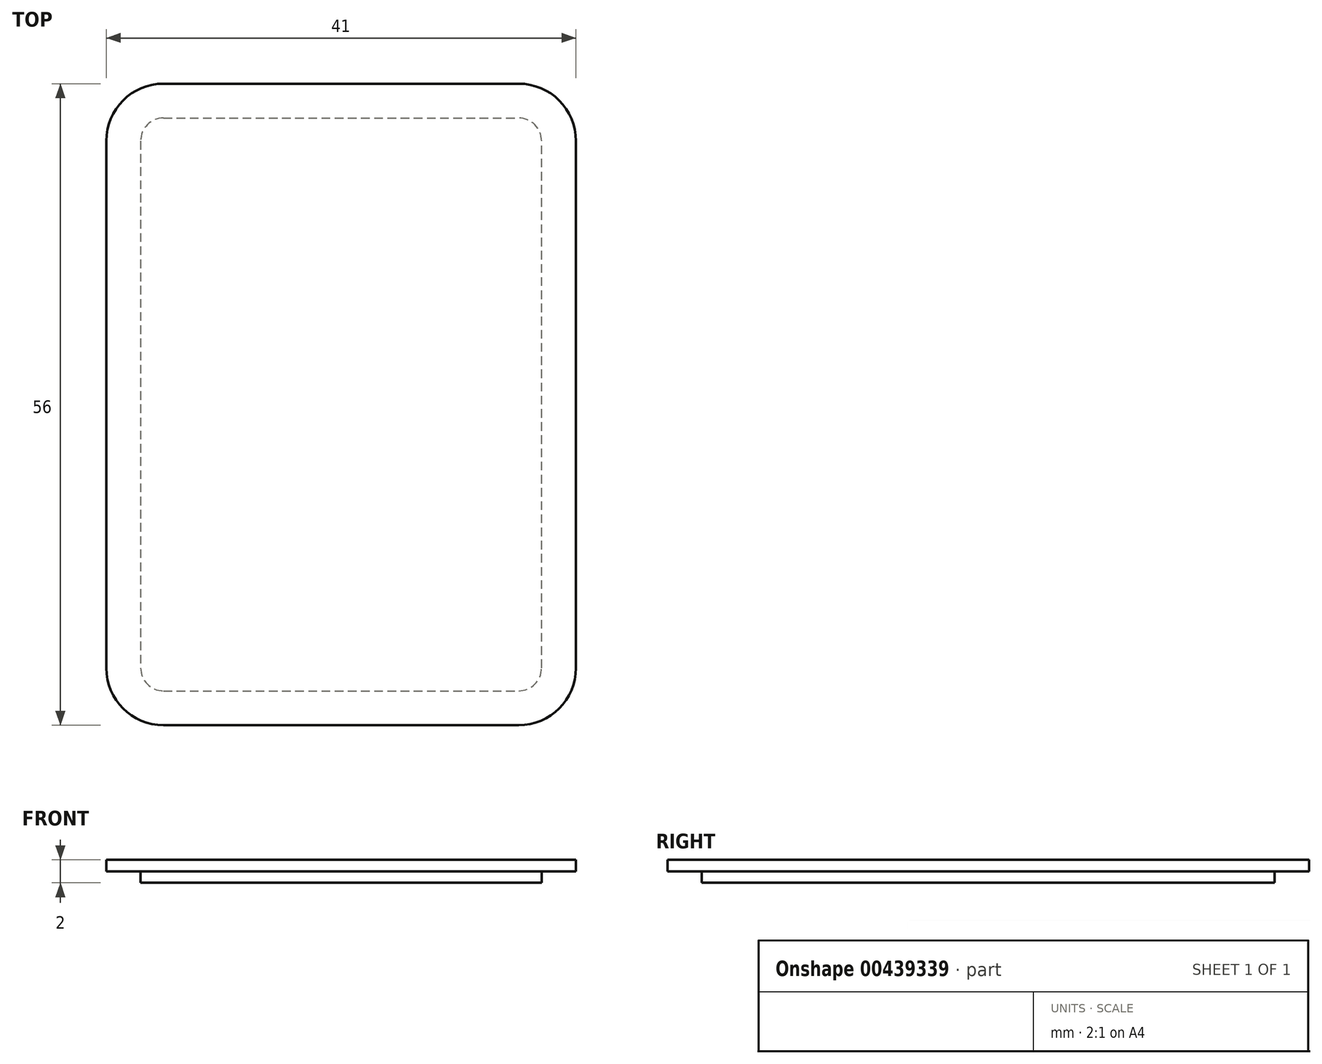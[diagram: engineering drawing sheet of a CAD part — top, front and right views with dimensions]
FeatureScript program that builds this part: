
annotation { "Feature Type Name" : "Feature", "Feature Type Description" : "" }
export const myFeature = defineFeature(function(context is Context, id is Id, definition is map)
    precondition{}
    {
        {
            var Q0;
            Q0=qCreatedBy(makeId("Top.planeOp"),FACE);
            var sketch = newSketch(context, id + "F0", { "sketchPlane" : qUnion([Q0])});
            skLineSegment(sketch, "E0.bottom", {"start": v(-15.75, -25) * mm, "end": v(15.25, -25) * mm});
            skLineSegment(sketch, "E0.top", {"start": v(-15.75, 25) * mm, "end": v(15.25, 25) * mm});
            skLineSegment(sketch, "E0.right", {"start": v(17.25, -23) * mm, "end": v(17.25, 23) * mm});
            skPoint(sketch, "E1.visualSharp", {"position": v(17.25, 25) * mm});
            skArc(sketch, "E1.filletArc", {"start": v(17.25, 23) * mm, "mid": v(16.67, 24.41) * mm, "end": v(15.25, 25) * mm});
            skPoint(sketch, "E2.visualSharp", {"position": v(17.25, -25) * mm});
            skArc(sketch, "E2.filletArc", {"start": v(15.25, -25) * mm, "mid": v(16.67, -24.41) * mm, "end": v(17.25, -23) * mm});
            skLineSegment(sketch, "E3", {"start": v(-17.75, 23) * mm, "end": v(-17.75, -23) * mm});
            skPoint(sketch, "E4.visualSharp", {"position": v(-17.75, 25) * mm});
            skArc(sketch, "E4.filletArc", {"start": v(-15.75, 25) * mm, "mid": v(-17.16, 24.41) * mm, "end": v(-17.75, 23) * mm});
            skPoint(sketch, "E5.visualSharp", {"position": v(-17.75, -25) * mm});
            skArc(sketch, "E5.filletArc", {"start": v(-17.75, -23) * mm, "mid": v(-17.16, -24.41) * mm, "end": v(-15.75, -25) * mm});
            skSolve(sketch);
        }
        {
            var Q0;
            Q0=makeQuery(id+"F0.imprint","IMPRINT",FACE,{"disambiguationData":[TD([[makeQuery(id+"F0.imprint","IMPRINT",EDGE,{"derivedFrom":sQuery(id+"F0.wireOp",EDGE,"E0.bottom")}),1.0]])]});
            extrude(context, id + "F1", {"entities" : qUnion([Q0]), "depth" : 2 * mm});
        }
        {
            var Q0;
            Q0=makeQuery(id+"F1.opExtrude","CAP_FACE",FACE,{"disambiguationData":[OSD([sQuery(id+"F0.wireOp",EDGE,"E0.bottom"),sQuery(id+"F0.wireOp",EDGE,"E0.top"),sQuery(id+"F0.wireOp",EDGE,"E0.right"),sQuery(id+"F0.wireOp",EDGE,"E1.filletArc"),sQuery(id+"F0.wireOp",EDGE,"E2.filletArc"),sQuery(id+"F0.wireOp",EDGE,"E3"),sQuery(id+"F0.wireOp",EDGE,"E4.filletArc"),sQuery(id+"F0.wireOp",EDGE,"E5.filletArc")])],"isStart":false});
            var sketch = newSketch(context, id + "F2", { "sketchPlane" : qUnion([Q0])});
            skArc(sketch, "E6.0", {"start": v(20.25, 23) * mm, "mid": v(18.79, 26.54) * mm, "end": v(15.25, 28) * mm});
            skLineSegment(sketch, "E6.1", {"start": v(20.25, -23) * mm, "end": v(20.25, 23) * mm});
            skLineSegment(sketch, "E6.2", {"start": v(15.25, 28) * mm, "end": v(-15.75, 28) * mm});
            skArc(sketch, "E6.3", {"start": v(15.25, -28) * mm, "mid": v(18.79, -26.54) * mm, "end": v(20.25, -23) * mm});
            skArc(sketch, "E6.4", {"start": v(-15.75, 28) * mm, "mid": v(-19.28, 26.54) * mm, "end": v(-20.75, 23) * mm});
            skLineSegment(sketch, "E6.5", {"start": v(-20.75, 23) * mm, "end": v(-20.75, -23) * mm});
            skArc(sketch, "E6.6", {"start": v(-20.75, -23) * mm, "mid": v(-19.28, -26.54) * mm, "end": v(-15.75, -28) * mm});
            skLineSegment(sketch, "E6.7", {"start": v(-15.75, -28) * mm, "end": v(15.25, -28) * mm});
            skSolve(sketch);
        }
        {
            var Q0;
            Q0 = qSketchRegion(id + "F2", true);
            extrude(context, id + "F3", {"entities" : qUnion([Q0]), "operationType" : NewBodyOperationType.ADD, "oppositeDirection" : true, "depth" : 1 * mm});
        }
    });
